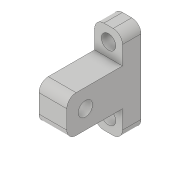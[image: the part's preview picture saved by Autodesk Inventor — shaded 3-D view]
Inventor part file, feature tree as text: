
AUTODESK INVENTOR PART (.ipt)
format: ipt  version: 2018 (Build 220112000, 112)  size: 142,848 bytes
history: native  units: in
note: dims shown in document units (in); Inventor stores cm internally (conversion verified against a paired STEP export)
features: sketch x4, extrude x2, fillet x2, hole x2
ambient origin geometry x8: Origin, YZ Plane, XZ Plane, XY Plane, X Axis, Y Axis, Z Axis, Center Point
bodies: Solid1 (feature_tree)
feature tree (10):
  extrude  "Extrusion1"  Depth=1.25in
  extrude  "Extrusion2"  Depth=0.375in
  fillet  "Fillet1"  Radius=0.375in
  fillet  "Fillet2"  Radius=0.75in
  hole  "Hole1"  [1 undecoded]
  hole  "Hole2"  [1 undecoded]
  sketch  "Sketch1"  dims[d0=0.375in d1=1.25in]
  sketch  "Sketch2"  dims[d2=1.0in d3=0.0in d4=0.375in d5=0.375in d6=0.75in]
  sketch  "Sketch3"  dims[d7=0.75in d8=1.0in d9=0.0in]
  sketch  "Sketch4"  dims[d10=0.125in d11=0.125in d12=0.25in d13=0.25in d14=0.75in d15=0.194in d16=0.75in d17=0.332in d18=0.25in d19=0.5635in d20=1.0in d21=0.8108in d22=0.1875in d23=0.1875in d24=0.1875in d25=0.1875in d26=0.1875in d27=0.1875in d28=0.875in d29=0.194in d30=0.75in d31=0.332in d32=0.25in d33=0.5635in d34=1.0in d35=0.8108in]
note: 2 required parameter values undecoded (feature->parameter linkage not recoverable at this tier; creation-order binding heuristic only, values carry confidence <= 0.55)
